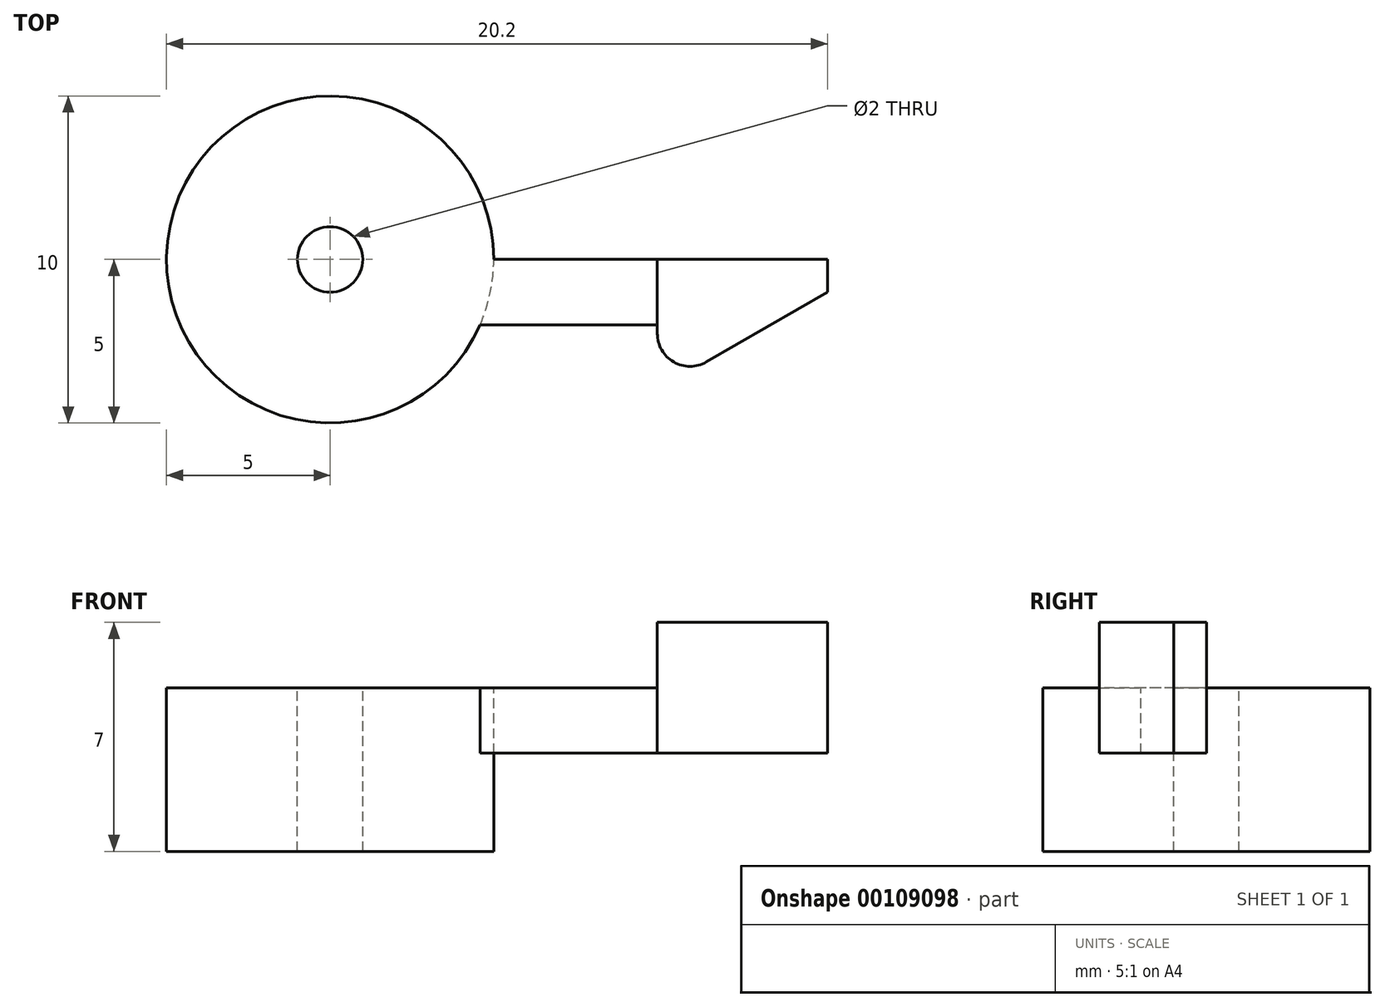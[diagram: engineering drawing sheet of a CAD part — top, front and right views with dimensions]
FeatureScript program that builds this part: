
annotation { "Feature Type Name" : "Feature", "Feature Type Description" : "" }
export const myFeature = defineFeature(function(context is Context, id is Id, definition is map)
    precondition{}
    {
        {
            var Q0;
            Q0=qCreatedBy(makeId("Top.planeOp"),FACE);
            var sketch = newSketch(context, id + "F0", { "sketchPlane" : qUnion([Q0])});
            skCircle(sketch, "E0", {"center": v(0, 0) * mm, "radius": 5 * mm});
            skLineSegment(sketch, "E1", {"start": v(5, 0) * mm, "end": v(10, 0) * mm});
            skLineSegment(sketch, "E2", {"start": v(15.2, 0) * mm, "end": v(10, 0) * mm});
            skLineSegment(sketch, "E3.MirrorCS", {"start": v(10, -2) * mm, "end": v(4.58, -2) * mm});
            skLineSegment(sketch, "E4.MirrorCS", {"start": v(10, -2) * mm, "end": v(10, -4) * mm});
            skLineSegment(sketch, "E5.MirrorCS", {"start": v(10, -4) * mm, "end": v(15.2, -1) * mm});
            skLineSegment(sketch, "E6.MirrorCS", {"start": v(10, 0) * mm, "end": v(10, -2) * mm});
            skLineSegment(sketch, "E7.MirrorCS", {"start": v(15.2, -1) * mm, "end": v(15.2, 0) * mm});
            skSolve(sketch);
        }
        {
            var Q0;
            {var subQ0=sQuery(id+"F0.wireOp",EDGE,"E0");var subQ1=makeQuery(id+"F0.imprint","INTERSECT",VERTEX,{"derivedFrom":[sQuery(id+"F0.wireOp",EDGE,"E1"),subQ0]});Q0=makeQuery(id+"F0.imprint","IMPRINT",FACE,{"disambiguationData":[TD([[makeQuery(id+"F0.imprint","IMPRINT",EDGE,{"disambiguationData":[TD([[subQ1,-1.0]])],"derivedFrom":subQ0}),1.0]])]});}
            extrude(context, id + "F1", {"entities" : qUnion([Q0]), "oppositeDirection" : true, "depth" : 5 * mm});
        }
        {
            var Q0;
            {var subQ0=sQuery(id+"F0.wireOp",EDGE,"E1");Q0=makeQuery(id+"F0.imprint","IMPRINT",FACE,{"disambiguationData":[TD([[makeQuery(id+"F0.imprint","IMPRINT",EDGE,{"derivedFrom":subQ0}),-1.0]])]});}
            extrude(context, id + "F2", {"entities" : qUnion([Q0]), "operationType" : NewBodyOperationType.ADD, "oppositeDirection" : true, "depth" : 2 * mm});
        }
        {
            var Q0;
            Q0=makeQuery(id+"F0.imprint","IMPRINT",FACE,{"disambiguationData":[TD([[makeQuery(id+"F0.imprint","IMPRINT",EDGE,{"derivedFrom":sQuery(id+"F0.wireOp",EDGE,"E2")}),1.0]])]});
            extrude(context, id + "F3", {"entities" : qUnion([Q0]), "operationType" : NewBodyOperationType.ADD, "endBound" : BoundingType.SYMMETRIC, "depth" : 4 * mm});
        }
        {
            var Q0;
            Q0=makeQuery(id+"F3.opExtrude","SWEPT_EDGE",EDGE,{"disambiguationData":[OSD([sQuery(id+"F0.wireOp",EDGE,"E4.MirrorCS"),sQuery(id+"F0.wireOp",EDGE,"E5.MirrorCS")])]});
            fillet(context, id + "F4", {"entities" : qUnion([Q0]), "radius" : 1 * mm, "tangentPropagation" : true, "allowEdgeOverflow" : false});
        }
        {
            var Q0;
            Q0=sQuery(id+"F0.wireOp",VERTEX,"E0.center");
            var Q1;
            Q1=makeQuery(id+"F1.opExtrude","SWEPT_BODY",BODY,{"disambiguationData":[OSD([sQuery(id+"F0.wireOp",EDGE,"E0")])]});
            hole(context, id + "F5", {"style" : HoleStyle.SIMPLE, "endStyle" : HoleEndStyle.THROUGH, "holeDiameter" : 2 * mm, "locations" : qUnion([Q0]), "scope" : qUnion([Q1]), "isTappedThrough" : true});
        }
    });
